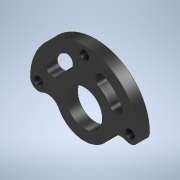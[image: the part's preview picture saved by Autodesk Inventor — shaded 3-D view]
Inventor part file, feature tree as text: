
AUTODESK INVENTOR PART (.ipt)
format: ipt  version: 2020 (Build 240168000, 168)  size: 188,928 bytes
history: native  units: in
note: dims shown in document units (in); Inventor stores cm internally (conversion verified against a paired STEP export)
features: extrude x2, sketch x2
ambient origin geometry x8: Origin, YZ Plane, XZ Plane, XY Plane, X Axis, Y Axis, Z Axis, Center Point
bodies: Solid1 (feature_tree)
feature tree (4):
  extrude  "Extrusion1"  Depth=0.25in
  extrude  "Extrusion2"  Depth=0.125in
  sketch  "Sketch1"  dims[d0=0.25in d1=0.0in d2=2.0in]
  sketch  "Sketch2"  dims[d3=0.7874in d6=0.205in d7=2.3622in d8=1.25in d9=0.25in d10=0.25in d11=0.25in d12=0.25in d13=0.125in d14=0.0in d15=0.0in]
